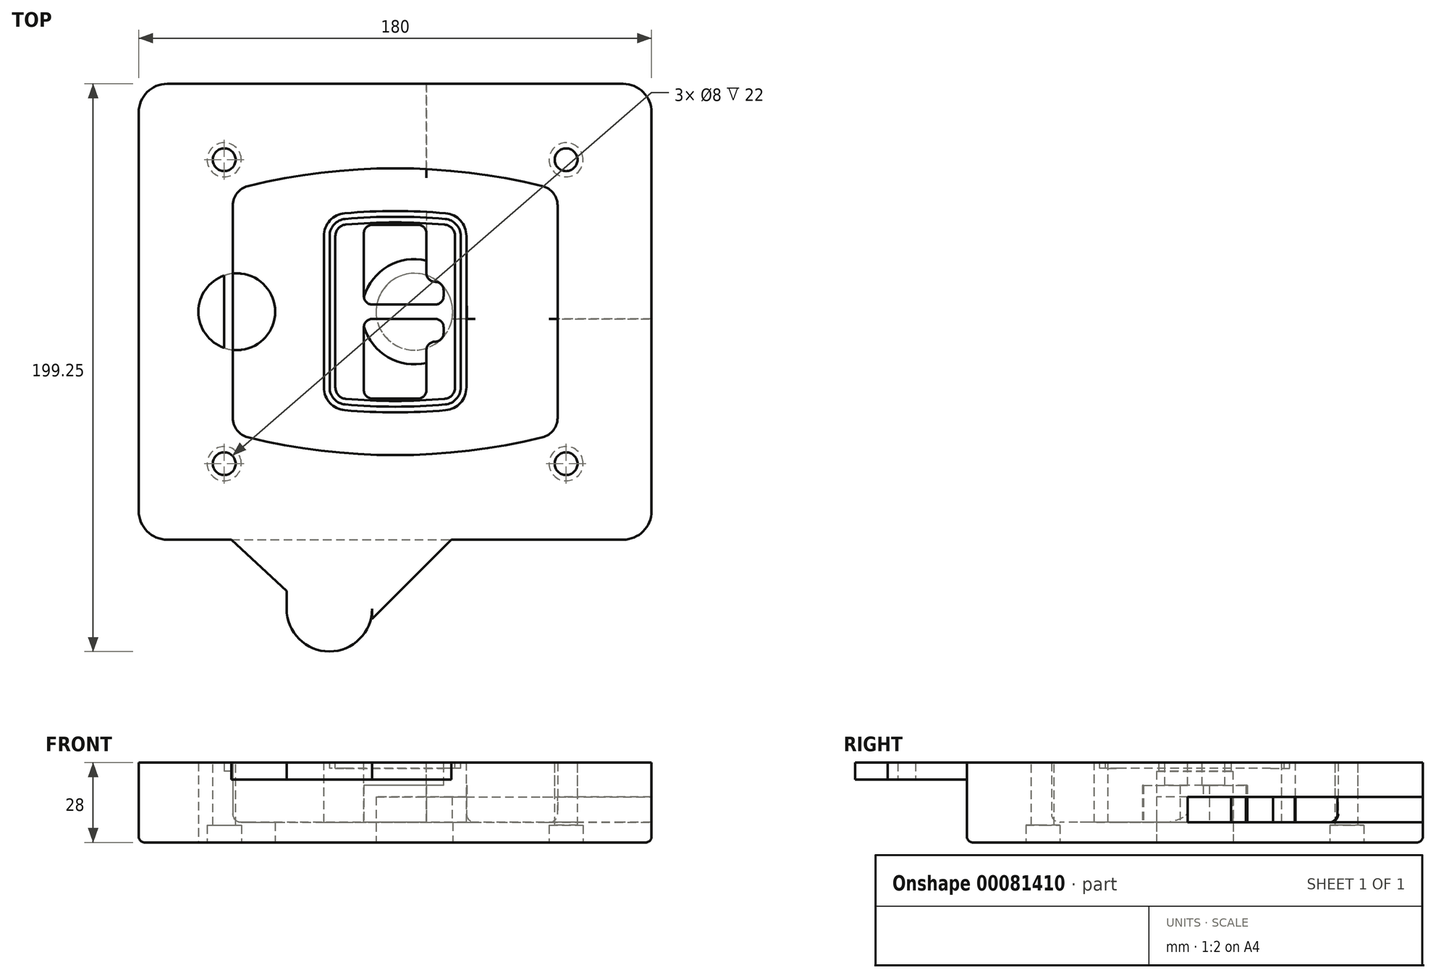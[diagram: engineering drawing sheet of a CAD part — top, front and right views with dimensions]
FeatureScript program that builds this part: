
annotation { "Feature Type Name" : "Feature", "Feature Type Description" : "" }
export const myFeature = defineFeature(function(context is Context, id is Id, definition is map)
    precondition{}
    {
        {
            var Q0;
            Q0=qCreatedBy(makeId("Top.planeOp"),FACE);
            var sketch = newSketch(context, id + "F0", { "sketchPlane" : qUnion([Q0])});
            skPoint(sketch, "E0.rect.middle", {"position": v(0, 0) * mm});
            skLineSegment(sketch, "E1.bottom", {"start": v(-80, -80) * mm, "end": v(80, -80) * mm});
            skLineSegment(sketch, "E1.top", {"start": v(-80, 80) * mm, "end": v(80, 80) * mm});
            skLineSegment(sketch, "E1.left", {"start": v(-90, -70) * mm, "end": v(-90, 70) * mm});
            skLineSegment(sketch, "E1.right", {"start": v(90, -70) * mm, "end": v(90, 70) * mm});
            skLineSegment(sketch, "E2", {"start": v(-90, 80) * mm, "end": v(90, -80) * mm, "construction": true});
            skLineSegment(sketch, "E3", {"start": v(90, 80) * mm, "end": v(-90, -80) * mm, "construction": true});
            skCircle(sketch, "E4", {"center": v(-60, 53.33) * mm, "radius": 4 * mm});
            skCircle(sketch, "E5", {"center": v(60, 53.33) * mm, "radius": 4 * mm});
            skCircle(sketch, "E6", {"center": v(60, -53.33) * mm, "radius": 4 * mm});
            skCircle(sketch, "E7", {"center": v(-60, -53.33) * mm, "radius": 4 * mm});
            skLineSegment(sketch, "E8", {"start": v(-60, 53.33) * mm, "end": v(60, 53.33) * mm, "construction": true});
            skLineSegment(sketch, "E9", {"start": v(60, 53.33) * mm, "end": v(60, -53.33) * mm, "construction": true});
            skLineSegment(sketch, "E10", {"start": v(60, -53.33) * mm, "end": v(-60, -53.33) * mm, "construction": true});
            skLineSegment(sketch, "E11", {"start": v(-60, -53.33) * mm, "end": v(-60, 53.33) * mm, "construction": true});
            skLineSegment(sketch, "E12", {"start": v(-60, 37.3) * mm, "end": v(-60, -37.3) * mm});
            skLineSegment(sketch, "E13", {"start": v(60, 37.3) * mm, "end": v(60, -37.3) * mm});
            skArc(sketch, "E14", {"start": v(52.38, 47.01) * mm, "mid": v(0, 53.33) * mm, "end": v(-52.38, 47.01) * mm});
            skArc(sketch, "E15", {"start": v(-52.38, -47.01) * mm, "mid": v(0, -53.33) * mm, "end": v(52.38, -47.01) * mm});
            skLineSegment(sketch, "E16", {"start": v(-60, 0) * mm, "end": v(60, 0) * mm, "construction": true});
            skPoint(sketch, "E17.visualSharp", {"position": v(-60, -45) * mm});
            skArc(sketch, "E17.filletArc", {"start": v(-60, -37.3) * mm, "mid": v(-57.87, -43.47) * mm, "end": v(-52.38, -47.01) * mm});
            skPoint(sketch, "E18.visualSharp", {"position": v(-60, 45) * mm});
            skArc(sketch, "E18.filletArc", {"start": v(-52.38, 47.01) * mm, "mid": v(-57.87, 43.47) * mm, "end": v(-60, 37.3) * mm});
            skPoint(sketch, "E19.visualSharp", {"position": v(60, 45) * mm});
            skArc(sketch, "E19.filletArc", {"start": v(60, 37.3) * mm, "mid": v(57.87, 43.47) * mm, "end": v(52.38, 47.01) * mm});
            skPoint(sketch, "E20.visualSharp", {"position": v(60, -45) * mm});
            skArc(sketch, "E20.filletArc", {"start": v(52.38, -47.01) * mm, "mid": v(57.87, -43.47) * mm, "end": v(60, -37.3) * mm});
            skPoint(sketch, "E21.visualSharp", {"position": v(-90, 80) * mm});
            skArc(sketch, "E21.filletArc", {"start": v(-80, 80) * mm, "mid": v(-87.07, 77.07) * mm, "end": v(-90, 70) * mm});
            skPoint(sketch, "E22.visualSharp", {"position": v(90, 80) * mm});
            skArc(sketch, "E22.filletArc", {"start": v(90, 70) * mm, "mid": v(87.07, 77.07) * mm, "end": v(80, 80) * mm});
            skPoint(sketch, "E23.visualSharp", {"position": v(90, -80) * mm});
            skArc(sketch, "E23.filletArc", {"start": v(80, -80) * mm, "mid": v(87.07, -77.07) * mm, "end": v(90, -70) * mm});
            skPoint(sketch, "E24.visualSharp", {"position": v(-90, -80) * mm});
            skArc(sketch, "E24.filletArc", {"start": v(-90, -70) * mm, "mid": v(-87.07, -77.07) * mm, "end": v(-80, -80) * mm});
            skArc(sketch, "E25.0", {"start": v(57, 37.3) * mm, "mid": v(55.5, 41.62) * mm, "end": v(51.67, 44.1) * mm});
            skLineSegment(sketch, "E25.1", {"start": v(57, 37.3) * mm, "end": v(57, -37.3) * mm});
            skArc(sketch, "E25.2", {"start": v(51.67, -44.1) * mm, "mid": v(55.5, -41.62) * mm, "end": v(57, -37.3) * mm});
            skArc(sketch, "E25.3", {"start": v(-51.67, -44.1) * mm, "mid": v(0, -50.33) * mm, "end": v(51.67, -44.1) * mm});
            skArc(sketch, "E25.4", {"start": v(-57, -37.3) * mm, "mid": v(-55.5, -41.62) * mm, "end": v(-51.67, -44.1) * mm});
            skArc(sketch, "E25.5", {"start": v(51.67, 44.1) * mm, "mid": v(0, 50.33) * mm, "end": v(-51.67, 44.1) * mm});
            skLineSegment(sketch, "E25.6", {"start": v(-57, 37.3) * mm, "end": v(-57, -37.3) * mm});
            skArc(sketch, "E25.7", {"start": v(-51.67, 44.1) * mm, "mid": v(-55.5, 41.62) * mm, "end": v(-57, 37.3) * mm});
            skArc(sketch, "E26.0", {"start": v(-53.33, 50.9) * mm, "mid": v(-61.01, 45.94) * mm, "end": v(-64, 37.3) * mm});
            skArc(sketch, "E26.1", {"start": v(53.33, 50.9) * mm, "mid": v(0, 57.33) * mm, "end": v(-53.33, 50.9) * mm});
            skArc(sketch, "E26.2", {"start": v(64, 37.3) * mm, "mid": v(61.01, 45.94) * mm, "end": v(53.33, 50.9) * mm});
            skLineSegment(sketch, "E26.3", {"start": v(64, 37.3) * mm, "end": v(64, -37.3) * mm});
            skArc(sketch, "E26.4", {"start": v(53.33, -50.9) * mm, "mid": v(61.01, -45.94) * mm, "end": v(64, -37.3) * mm});
            skLineSegment(sketch, "E26.5", {"start": v(-64, 37.3) * mm, "end": v(-64, -37.3) * mm});
            skArc(sketch, "E26.6", {"start": v(-53.33, -50.9) * mm, "mid": v(0, -57.33) * mm, "end": v(53.33, -50.9) * mm});
            skArc(sketch, "E26.7", {"start": v(-64, -37.3) * mm, "mid": v(-61.01, -45.94) * mm, "end": v(-53.33, -50.9) * mm});
            skSolve(sketch);
        }
        {
            var Q0;
            Q0=makeQuery(id+"F0.imprint","IMPRINT",FACE,{"disambiguationData":[TD([[makeQuery(id+"F0.imprint","IMPRINT",EDGE,{"derivedFrom":sQuery(id+"F0.wireOp",EDGE,"E1.bottom")}),1.0]])]});
            var Q1;
            Q1=makeQuery(id+"F0.imprint","IMPRINT",FACE,{"disambiguationData":[TD([[makeQuery(id+"F0.imprint","IMPRINT",EDGE,{"derivedFrom":sQuery(id+"F0.wireOp",EDGE,"E12")}),1.0]])]});
            var Q2;
            Q2=makeQuery(id+"F0.imprint","IMPRINT",FACE,{"disambiguationData":[TD([[makeQuery(id+"F0.imprint","IMPRINT",EDGE,{"derivedFrom":sQuery(id+"F0.wireOp",EDGE,"E25.0")}),1.0]])]});
            var Q3;
            Q3=makeQuery(id+"F0.imprint","IMPRINT",FACE,{"disambiguationData":[TD([[makeQuery(id+"F0.imprint","IMPRINT",EDGE,{"derivedFrom":sQuery(id+"F0.wireOp",EDGE,"E12")}),-1.0]])]});
            extrude(context, id + "F1", {"entities" : qUnion([Q0, Q1, Q2, Q3]), "oppositeDirection" : true, "depth" : 25 * mm});
        }
        {
            var Q0;
            Q0=makeQuery(id+"F0.imprint","IMPRINT",FACE,{"disambiguationData":[TD([[makeQuery(id+"F0.imprint","IMPRINT",EDGE,{"derivedFrom":sQuery(id+"F0.wireOp",EDGE,"E12")}),1.0]])]});
            extrude(context, id + "F2", {"entities" : qUnion([Q0]), "operationType" : NewBodyOperationType.ADD, "depth" : 3 * mm});
        }
        {
            var Q0;
            Q0=makeQuery(id+"F0.imprint","IMPRINT",FACE,{"disambiguationData":[TD([[makeQuery(id+"F0.imprint","IMPRINT",EDGE,{"derivedFrom":sQuery(id+"F0.wireOp",EDGE,"E25.0")}),1.0]])]});
            extrude(context, id + "F3", {"entities" : qUnion([Q0]), "operationType" : NewBodyOperationType.REMOVE, "oppositeDirection" : true, "depth" : 18 * mm});
        }
        {
            var Q0;
            Q0=makeQuery(id+"F2.opExtrude","CAP_FACE",FACE,{"disambiguationData":[OSD([sQuery(id+"F0.wireOp",EDGE,"E12"),sQuery(id+"F0.wireOp",EDGE,"E13"),sQuery(id+"F0.wireOp",EDGE,"E14"),sQuery(id+"F0.wireOp",EDGE,"E15"),sQuery(id+"F0.wireOp",EDGE,"E17.filletArc"),sQuery(id+"F0.wireOp",EDGE,"E18.filletArc"),sQuery(id+"F0.wireOp",EDGE,"E19.filletArc"),sQuery(id+"F0.wireOp",EDGE,"E20.filletArc"),sQuery(id+"F0.wireOp",EDGE,"E25.0"),sQuery(id+"F0.wireOp",EDGE,"E25.1"),sQuery(id+"F0.wireOp",EDGE,"E25.2"),sQuery(id+"F0.wireOp",EDGE,"E25.3"),sQuery(id+"F0.wireOp",EDGE,"E25.4"),sQuery(id+"F0.wireOp",EDGE,"E25.5"),sQuery(id+"F0.wireOp",EDGE,"E25.6"),sQuery(id+"F0.wireOp",EDGE,"E25.7")])],"isStart":false});
            var sketch = newSketch(context, id + "F4", { "sketchPlane" : qUnion([Q0])});
            skArc(sketch, "E27.0", {"start": v(-17.7, -34.56) * mm, "mid": v(0, -35.33) * mm, "end": v(17.7, -34.56) * mm});
            skArc(sketch, "E28.0", {"start": v(17.7, 34.56) * mm, "mid": v(0, 35.33) * mm, "end": v(-17.7, 34.56) * mm});
            skLineSegment(sketch, "E29", {"start": v(-25, 26.59) * mm, "end": v(-25, -26.59) * mm});
            skLineSegment(sketch, "E30", {"start": v(25, 26.59) * mm, "end": v(25, -26.59) * mm});
            skLineSegment(sketch, "E31", {"start": v(-25, 33.78) * mm, "end": v(25, 33.78) * mm, "construction": true});
            skLineSegment(sketch, "E32", {"start": v(-25, -33.78) * mm, "end": v(25, -33.78) * mm, "construction": true});
            skPoint(sketch, "E33.visualSharp", {"position": v(-25, 33.78) * mm});
            skArc(sketch, "E33.filletArc", {"start": v(-17.7, 34.56) * mm, "mid": v(-22.9, 32) * mm, "end": v(-25, 26.59) * mm});
            skPoint(sketch, "E34.visualSharp", {"position": v(25, 33.78) * mm});
            skArc(sketch, "E34.filletArc", {"start": v(25, 26.59) * mm, "mid": v(22.9, 32) * mm, "end": v(17.7, 34.56) * mm});
            skPoint(sketch, "E35.visualSharp", {"position": v(25, -33.78) * mm});
            skArc(sketch, "E35.filletArc", {"start": v(17.7, -34.56) * mm, "mid": v(22.9, -32) * mm, "end": v(25, -26.59) * mm});
            skPoint(sketch, "E36.visualSharp", {"position": v(-25, -33.78) * mm});
            skArc(sketch, "E36.filletArc", {"start": v(-25, -26.59) * mm, "mid": v(-22.9, -32) * mm, "end": v(-17.7, -34.56) * mm});
            skArc(sketch, "E37.0", {"start": v(51.67, 44.1) * mm, "mid": v(0, 50.33) * mm, "end": v(-51.67, 44.1) * mm});
            skArc(sketch, "E37.1", {"start": v(-51.67, 44.1) * mm, "mid": v(-55.5, 41.62) * mm, "end": v(-57, 37.3) * mm});
            skLineSegment(sketch, "E37.2", {"start": v(-57, 37.3) * mm, "end": v(-57, -37.3) * mm});
            skArc(sketch, "E37.3", {"start": v(-57, -37.3) * mm, "mid": v(-55.5, -41.62) * mm, "end": v(-51.67, -44.1) * mm});
            skArc(sketch, "E37.4", {"start": v(-51.67, -44.1) * mm, "mid": v(0, -50.33) * mm, "end": v(51.67, -44.1) * mm});
            skArc(sketch, "E37.5", {"start": v(51.67, -44.1) * mm, "mid": v(55.5, -41.62) * mm, "end": v(57, -37.3) * mm});
            skLineSegment(sketch, "E37.6", {"start": v(57, 37.3) * mm, "end": v(57, -37.3) * mm});
            skArc(sketch, "E37.7", {"start": v(57, 37.3) * mm, "mid": v(55.5, 41.62) * mm, "end": v(51.67, 44.1) * mm});
            skLineSegment(sketch, "E38.0", {"start": v(23, 26.59) * mm, "end": v(23, -26.59) * mm});
            skArc(sketch, "E38.1", {"start": v(17.53, -32.56) * mm, "mid": v(21.42, -30.64) * mm, "end": v(23, -26.59) * mm});
            skArc(sketch, "E38.2", {"start": v(-17.53, -32.56) * mm, "mid": v(0, -33.33) * mm, "end": v(17.53, -32.56) * mm});
            skArc(sketch, "E38.3", {"start": v(-23, -26.59) * mm, "mid": v(-21.42, -30.64) * mm, "end": v(-17.53, -32.56) * mm});
            skLineSegment(sketch, "E38.4", {"start": v(-23, 26.59) * mm, "end": v(-23, -26.59) * mm});
            skArc(sketch, "E38.5", {"start": v(23, 26.59) * mm, "mid": v(21.42, 30.64) * mm, "end": v(17.53, 32.56) * mm});
            skArc(sketch, "E38.6", {"start": v(-17.53, 32.56) * mm, "mid": v(-21.42, 30.64) * mm, "end": v(-23, 26.59) * mm});
            skArc(sketch, "E38.7", {"start": v(17.53, 32.56) * mm, "mid": v(0, 33.33) * mm, "end": v(-17.53, 32.56) * mm});
            skArc(sketch, "E39.0", {"start": v(21, 26.59) * mm, "mid": v(19.95, 29.29) * mm, "end": v(17.35, 30.57) * mm});
            skLineSegment(sketch, "E39.1", {"start": v(21, 26.59) * mm, "end": v(21, -26.59) * mm});
            skArc(sketch, "E39.2", {"start": v(17.35, -30.57) * mm, "mid": v(19.95, -29.29) * mm, "end": v(21, -26.59) * mm});
            skArc(sketch, "E39.3", {"start": v(-17.35, -30.57) * mm, "mid": v(0, -31.33) * mm, "end": v(17.35, -30.57) * mm});
            skArc(sketch, "E39.4", {"start": v(-21, -26.59) * mm, "mid": v(-19.95, -29.29) * mm, "end": v(-17.35, -30.57) * mm});
            skArc(sketch, "E39.5", {"start": v(17.35, 30.57) * mm, "mid": v(0, 31.33) * mm, "end": v(-17.35, 30.57) * mm});
            skLineSegment(sketch, "E39.6", {"start": v(-21, 26.59) * mm, "end": v(-21, -26.59) * mm});
            skArc(sketch, "E39.7", {"start": v(-17.35, 30.57) * mm, "mid": v(-19.95, 29.29) * mm, "end": v(-21, 26.59) * mm});
            skLineSegment(sketch, "E40", {"start": v(-25, 0) * mm, "end": v(25, 0) * mm, "construction": true});
            skLineSegment(sketch, "E41", {"start": v(-11, 5.5) * mm, "end": v(-11, 27.5) * mm});
            skLineSegment(sketch, "E42", {"start": v(-8, 30.5) * mm, "end": v(8, 30.5) * mm});
            skLineSegment(sketch, "E43", {"start": v(11, 27.5) * mm, "end": v(11, 13.5) * mm});
            skLineSegment(sketch, "E44", {"start": v(14, 10.5) * mm, "end": v(14, 10.5) * mm});
            skLineSegment(sketch, "E45", {"start": v(17, 7.5) * mm, "end": v(17, 5.5) * mm});
            skLineSegment(sketch, "E46", {"start": v(14, 2.5) * mm, "end": v(-8, 2.5) * mm});
            skPoint(sketch, "E47.visualSharp", {"position": v(-11, 30.5) * mm});
            skArc(sketch, "E47.filletArc", {"start": v(-8, 30.5) * mm, "mid": v(-10.12, 29.62) * mm, "end": v(-11, 27.5) * mm});
            skPoint(sketch, "E48.visualSharp", {"position": v(11, 30.5) * mm});
            skArc(sketch, "E48.filletArc", {"start": v(11, 27.5) * mm, "mid": v(10.12, 29.62) * mm, "end": v(8, 30.5) * mm});
            skPoint(sketch, "E49.visualSharp", {"position": v(11, 10.5) * mm});
            skArc(sketch, "E49.filletArc", {"start": v(11, 13.5) * mm, "mid": v(11.88, 11.38) * mm, "end": v(14, 10.5) * mm});
            skPoint(sketch, "E50.visualSharp", {"position": v(17, 10.5) * mm});
            skArc(sketch, "E50.filletArc", {"start": v(17, 7.5) * mm, "mid": v(16.12, 9.62) * mm, "end": v(14, 10.5) * mm});
            skPoint(sketch, "E51.visualSharp", {"position": v(17, 2.5) * mm});
            skArc(sketch, "E51.filletArc", {"start": v(14, 2.5) * mm, "mid": v(16.12, 3.38) * mm, "end": v(17, 5.5) * mm});
            skPoint(sketch, "E52.visualSharp", {"position": v(-11, 2.5) * mm});
            skArc(sketch, "E52.filletArc", {"start": v(-11, 5.5) * mm, "mid": v(-10.12, 3.38) * mm, "end": v(-8, 2.5) * mm});
            skLineSegment(sketch, "E53.0.MirrorCS", {"start": v(14, -2.5) * mm, "end": v(-8, -2.5) * mm});
            skArc(sketch, "E54.0.MirrorCS", {"start": v(-11, -5.5) * mm, "mid": v(-10.12, -3.38) * mm, "end": v(-8, -2.5) * mm});
            skLineSegment(sketch, "E55.0.MirrorCS", {"start": v(-11, -5.5) * mm, "end": v(-11, -27.5) * mm});
            skArc(sketch, "E56.0.MirrorCS", {"start": v(-8, -30.5) * mm, "mid": v(-10.12, -29.62) * mm, "end": v(-11, -27.5) * mm});
            skLineSegment(sketch, "E57.0.MirrorCS", {"start": v(-8, -30.5) * mm, "end": v(8, -30.5) * mm});
            skArc(sketch, "E58.0.MirrorCS", {"start": v(11, -27.5) * mm, "mid": v(10.12, -29.62) * mm, "end": v(8, -30.5) * mm});
            skLineSegment(sketch, "E59.0.MirrorCS", {"start": v(11, -27.5) * mm, "end": v(11, -13.5) * mm});
            skArc(sketch, "E60.0.MirrorCS", {"start": v(11, -13.5) * mm, "mid": v(11.88, -11.38) * mm, "end": v(14, -10.5) * mm});
            skArc(sketch, "E61.0.MirrorCS", {"start": v(17, -7.5) * mm, "mid": v(16.12, -9.62) * mm, "end": v(14, -10.5) * mm});
            skLineSegment(sketch, "E62.0.MirrorCS", {"start": v(17, -7.5) * mm, "end": v(17, -5.5) * mm});
            skArc(sketch, "E63.0.MirrorCS", {"start": v(14, -2.5) * mm, "mid": v(16.12, -3.38) * mm, "end": v(17, -5.5) * mm});
            skSolve(sketch);
        }
        {
            var Q0;
            Q0=makeQuery(id+"F4.imprint","IMPRINT",FACE,{"disambiguationData":[TD([[makeQuery(id+"F4.imprint","IMPRINT",EDGE,{"derivedFrom":sQuery(id+"F4.wireOp",EDGE,"E27.0")}),1.0]])]});
            var Q1;
            Q1=makeQuery(id+"F4.imprint","IMPRINT",FACE,{"disambiguationData":[TD([[makeQuery(id+"F4.imprint","IMPRINT",EDGE,{"derivedFrom":sQuery(id+"F4.wireOp",EDGE,"E38.0")}),-1.0]])]});
            var Q2;
            Q2=makeQuery(id+"F4.imprint","IMPRINT",FACE,{"disambiguationData":[TD([[makeQuery(id+"F4.imprint","IMPRINT",EDGE,{"derivedFrom":sQuery(id+"F4.wireOp",EDGE,"E39.0")}),1.0]])]});
            extrude(context, id + "F5", {"entities" : qUnion([Q0, Q1, Q2]), "operationType" : NewBodyOperationType.ADD, "endBound" : BoundingType.UP_TO_NEXT, "oppositeDirection" : true, "depth" : 25 * mm});
        }
        {
            var Q0;
            Q0=makeQuery(id+"F4.imprint","IMPRINT",FACE,{"disambiguationData":[TD([[makeQuery(id+"F4.imprint","IMPRINT",EDGE,{"derivedFrom":sQuery(id+"F4.wireOp",EDGE,"E38.0")}),-1.0]])]});
            extrude(context, id + "F6", {"entities" : qUnion([Q0]), "operationType" : NewBodyOperationType.REMOVE, "oppositeDirection" : true, "depth" : 2 * mm});
        }
        {
            var Q0;
            Q0=makeQuery(id+"F1.opExtrude","CAP_FACE",FACE,{"disambiguationData":[OSD([sQuery(id+"F0.wireOp",EDGE,"E1.bottom"),sQuery(id+"F0.wireOp",EDGE,"E1.top"),sQuery(id+"F0.wireOp",EDGE,"E1.left"),sQuery(id+"F0.wireOp",EDGE,"E1.right"),sQuery(id+"F0.wireOp",EDGE,"E4"),sQuery(id+"F0.wireOp",EDGE,"E5"),sQuery(id+"F0.wireOp",EDGE,"E6"),sQuery(id+"F0.wireOp",EDGE,"E7"),sQuery(id+"F0.wireOp",EDGE,"E21.filletArc"),sQuery(id+"F0.wireOp",EDGE,"E22.filletArc"),sQuery(id+"F0.wireOp",EDGE,"E23.filletArc"),sQuery(id+"F0.wireOp",EDGE,"E24.filletArc")])],"isStart":false});
            var sketch = newSketch(context, id + "F7", { "sketchPlane" : qUnion([Q0])});
            skCircle(sketch, "E64", {"center": v(6.76, 0) * mm, "radius": 13.47 * mm});
            skCircle(sketch, "E65", {"center": v(-55.56, 0) * mm, "radius": 13.47 * mm});
            skLineSegment(sketch, "E66", {"start": v(90, 0) * mm, "end": v(-90, 0) * mm});
            skCircle(sketch, "E67", {"center": v(6.76, 0) * mm, "radius": 18.47 * mm});
            skCircle(sketch, "E68", {"center": v(60, -53.33) * mm, "radius": 6 * mm});
            skCircle(sketch, "E69", {"center": v(-60, -53.33) * mm, "radius": 6 * mm});
            skCircle(sketch, "E70", {"center": v(-60, 53.33) * mm, "radius": 6 * mm});
            skCircle(sketch, "E71", {"center": v(60, 53.33) * mm, "radius": 6 * mm});
            skSolve(sketch);
        }
        {
            var Q0;
            {var subQ1=sQuery(id+"F7.wireOp",EDGE,"E66");var subQ4=sQuery(id+"F7.wireOp",EDGE,"E64");var subQ6=makeQuery(id+"F7.imprint","INTERSECT",VERTEX,{"disambiguationData":[OD(0.0)],"derivedFrom":[subQ4,subQ1]});Q0=makeQuery(id+"F7.imprint","IMPRINT",FACE,{"disambiguationData":[TD([[makeQuery(id+"F7.imprint","IMPRINT",EDGE,{"disambiguationData":[TD([[subQ6,-1.0]])],"derivedFrom":subQ4}),-1.0]])]});}
            var Q1;
            {var subQ0=sQuery(id+"F7.wireOp",EDGE,"E66");var subQ1=sQuery(id+"F7.wireOp",EDGE,"E64");var subQ3=makeQuery(id+"F7.imprint","INTERSECT",VERTEX,{"disambiguationData":[OD(0.0)],"derivedFrom":[subQ1,subQ0]});Q1=makeQuery(id+"F7.imprint","IMPRINT",FACE,{"disambiguationData":[TD([[makeQuery(id+"F7.imprint","IMPRINT",EDGE,{"disambiguationData":[TD([[subQ3,-1.0]])],"derivedFrom":subQ1}),1.0]])]});}
            var Q2;
            {var subQ0=sQuery(id+"F7.wireOp",EDGE,"E66");var subQ1=sQuery(id+"F7.wireOp",EDGE,"E64");var subQ3=makeQuery(id+"F7.imprint","INTERSECT",VERTEX,{"disambiguationData":[OD(0.0)],"derivedFrom":[subQ1,subQ0]});Q2=makeQuery(id+"F7.imprint","IMPRINT",FACE,{"disambiguationData":[TD([[makeQuery(id+"F7.imprint","IMPRINT",EDGE,{"disambiguationData":[TD([[subQ3,1.0]])],"derivedFrom":subQ1}),1.0]])]});}
            var Q3;
            {var subQ1=sQuery(id+"F7.wireOp",EDGE,"E66");var subQ4=sQuery(id+"F7.wireOp",EDGE,"E64");var subQ6=makeQuery(id+"F7.imprint","INTERSECT",VERTEX,{"disambiguationData":[OD(0.0)],"derivedFrom":[subQ4,subQ1]});Q3=makeQuery(id+"F7.imprint","IMPRINT",FACE,{"disambiguationData":[TD([[makeQuery(id+"F7.imprint","IMPRINT",EDGE,{"disambiguationData":[TD([[subQ6,1.0]])],"derivedFrom":subQ4}),-1.0]])]});}
            extrude(context, id + "F8", {"entities" : qUnion([Q0, Q1, Q2, Q3]), "operationType" : NewBodyOperationType.ADD, "oppositeDirection" : true, "depth" : 20 * mm});
        }
        {
            var Q0;
            {var subQ0=sQuery(id+"F7.wireOp",EDGE,"E66");var subQ1=sQuery(id+"F7.wireOp",EDGE,"E64");var subQ3=makeQuery(id+"F7.imprint","INTERSECT",VERTEX,{"disambiguationData":[OD(0.0)],"derivedFrom":[subQ1,subQ0]});Q0=makeQuery(id+"F7.imprint","IMPRINT",FACE,{"disambiguationData":[TD([[makeQuery(id+"F7.imprint","IMPRINT",EDGE,{"disambiguationData":[TD([[subQ3,-1.0]])],"derivedFrom":subQ1}),1.0]])]});}
            var Q1;
            {var subQ0=sQuery(id+"F7.wireOp",EDGE,"E66");var subQ1=sQuery(id+"F7.wireOp",EDGE,"E64");var subQ3=makeQuery(id+"F7.imprint","INTERSECT",VERTEX,{"disambiguationData":[OD(0.0)],"derivedFrom":[subQ1,subQ0]});Q1=makeQuery(id+"F7.imprint","IMPRINT",FACE,{"disambiguationData":[TD([[makeQuery(id+"F7.imprint","IMPRINT",EDGE,{"disambiguationData":[TD([[subQ3,1.0]])],"derivedFrom":subQ1}),1.0]])]});}
            extrude(context, id + "F9", {"entities" : qUnion([Q0, Q1]), "operationType" : NewBodyOperationType.REMOVE, "oppositeDirection" : true, "depth" : 16 * mm});
        }
        {
            var Q0;
            {var subQ0=sQuery(id+"F7.wireOp",EDGE,"E66");var subQ1=sQuery(id+"F7.wireOp",EDGE,"E65");var subQ3=makeQuery(id+"F7.imprint","INTERSECT",VERTEX,{"disambiguationData":[OD(0.0)],"derivedFrom":[subQ1,subQ0]});Q0=makeQuery(id+"F7.imprint","IMPRINT",FACE,{"disambiguationData":[TD([[makeQuery(id+"F7.imprint","IMPRINT",EDGE,{"disambiguationData":[TD([[subQ3,-1.0]])],"derivedFrom":subQ1}),1.0]])]});}
            var Q1;
            {var subQ0=sQuery(id+"F7.wireOp",EDGE,"E66");var subQ1=sQuery(id+"F7.wireOp",EDGE,"E65");var subQ3=makeQuery(id+"F7.imprint","INTERSECT",VERTEX,{"disambiguationData":[OD(0.0)],"derivedFrom":[subQ1,subQ0]});Q1=makeQuery(id+"F7.imprint","IMPRINT",FACE,{"disambiguationData":[TD([[makeQuery(id+"F7.imprint","IMPRINT",EDGE,{"disambiguationData":[TD([[subQ3,1.0]])],"derivedFrom":subQ1}),1.0]])]});}
            extrude(context, id + "F10", {"entities" : qUnion([Q0, Q1]), "operationType" : NewBodyOperationType.REMOVE, "oppositeDirection" : true, "depth" : 25 * mm});
        }
        {
            var Q0;
            Q0=makeQuery(id+"F7.imprint","IMPRINT",FACE,{"disambiguationData":[TD([[makeQuery(id+"F7.imprint","IMPRINT",EDGE,{"derivedFrom":sQuery(id+"F7.wireOp",EDGE,"E68")}),1.0]])]});
            var Q1;
            Q1=makeQuery(id+"F7.imprint","IMPRINT",FACE,{"disambiguationData":[TD([[makeQuery(id+"F7.imprint","IMPRINT",EDGE,{"derivedFrom":makeQuery(id+"F1.opExtrude","CAP_EDGE",EDGE,{"disambiguationData":[OSD([sQuery(id+"F0.wireOp",EDGE,"E5")])],"isStart":false})}),-1.0]])]});
            var Q2;
            Q2=makeQuery(id+"F7.imprint","IMPRINT",FACE,{"disambiguationData":[TD([[makeQuery(id+"F7.imprint","IMPRINT",EDGE,{"derivedFrom":sQuery(id+"F7.wireOp",EDGE,"E69")}),1.0]])]});
            var Q3;
            Q3=makeQuery(id+"F7.imprint","IMPRINT",FACE,{"disambiguationData":[TD([[makeQuery(id+"F7.imprint","IMPRINT",EDGE,{"derivedFrom":makeQuery(id+"F1.opExtrude","CAP_EDGE",EDGE,{"disambiguationData":[OSD([sQuery(id+"F0.wireOp",EDGE,"E4")])],"isStart":false})}),-1.0]])]});
            var Q4;
            Q4=makeQuery(id+"F7.imprint","IMPRINT",FACE,{"disambiguationData":[TD([[makeQuery(id+"F7.imprint","IMPRINT",EDGE,{"derivedFrom":sQuery(id+"F7.wireOp",EDGE,"E70")}),1.0]])]});
            var Q5;
            Q5=makeQuery(id+"F7.imprint","IMPRINT",FACE,{"disambiguationData":[TD([[makeQuery(id+"F7.imprint","IMPRINT",EDGE,{"derivedFrom":makeQuery(id+"F1.opExtrude","CAP_EDGE",EDGE,{"disambiguationData":[OSD([sQuery(id+"F0.wireOp",EDGE,"E7")])],"isStart":false})}),-1.0]])]});
            var Q6;
            Q6=makeQuery(id+"F7.imprint","IMPRINT",FACE,{"disambiguationData":[TD([[makeQuery(id+"F7.imprint","IMPRINT",EDGE,{"derivedFrom":sQuery(id+"F7.wireOp",EDGE,"E71")}),1.0]])]});
            var Q7;
            Q7=makeQuery(id+"F7.imprint","IMPRINT",FACE,{"disambiguationData":[TD([[makeQuery(id+"F7.imprint","IMPRINT",EDGE,{"derivedFrom":makeQuery(id+"F1.opExtrude","CAP_EDGE",EDGE,{"disambiguationData":[OSD([sQuery(id+"F0.wireOp",EDGE,"E6")])],"isStart":false})}),-1.0]])]});
            extrude(context, id + "F11", {"entities" : qUnion([Q0, Q1, Q2, Q3, Q4, Q5, Q6, Q7]), "operationType" : NewBodyOperationType.REMOVE, "oppositeDirection" : true, "depth" : 6 * mm});
        }
        {
            var Q0;
            Q0=makeQuery(id+"F9.boolean.opBoolean","COPY",FACE,{"derivedFrom":makeQuery(id+"F9.opExtrude","CAP_FACE",FACE,{"disambiguationData":[OSD([sQuery(id+"F7.wireOp",EDGE,"E64")])],"isStart":false})});
            var sketch = newSketch(context, id + "F12", { "sketchPlane" : qUnion([Q0])});
            skArc(sketch, "E72.0", {"start": v(11, -88.19) * mm, "mid": v(97.1, -83.6) * mm, "end": v(92.5, 2.5) * mm});
            skLineSegment(sketch, "E72.1", {"start": v(11, -17.97) * mm, "end": v(11, -17.97) * mm});
            skLineSegment(sketch, "E73", {"start": v(92.5, -105.13) * mm, "end": v(102.3, -105.13) * mm});
            skLineSegment(sketch, "E74.0", {"start": v(92.5, 2.5) * mm, "end": v(14, 2.5) * mm});
            skArc(sketch, "E74.1", {"start": v(14, 2.5) * mm, "mid": v(16.12, 3.38) * mm, "end": v(17, 5.5) * mm});
            skLineSegment(sketch, "E74.2", {"start": v(17, 7.5) * mm, "end": v(17, 5.5) * mm});
            skArc(sketch, "E74.3", {"start": v(17, 7.5) * mm, "mid": v(16.12, 9.62) * mm, "end": v(14, 10.5) * mm});
            skArc(sketch, "E74.4", {"start": v(11, 13.5) * mm, "mid": v(11.88, 11.38) * mm, "end": v(14, 10.5) * mm});
            skLineSegment(sketch, "E74.5", {"start": v(11, 13.5) * mm, "end": v(11, -88.19) * mm});
            skLineSegment(sketch, "E74.7", {"start": v(92.5, -2.5) * mm, "end": v(14, -2.5) * mm});
            skArc(sketch, "E74.8", {"start": v(14, -2.5) * mm, "mid": v(16.12, -3.38) * mm, "end": v(17, -5.5) * mm});
            skLineSegment(sketch, "E74.9", {"start": v(17, -7.5) * mm, "end": v(17, -5.5) * mm});
            skArc(sketch, "E74.10", {"start": v(17, -7.5) * mm, "mid": v(16.12, -9.62) * mm, "end": v(14, -10.5) * mm});
            skArc(sketch, "E74.11", {"start": v(11, -13.5) * mm, "mid": v(11.88, -11.38) * mm, "end": v(14, -10.5) * mm});
            skLineSegment(sketch, "E74.12", {"start": v(11, -17.97) * mm, "end": v(11, -13.5) * mm});
            skPoint(sketch, "E75.orphan", {"position": v(11, -27.5) * mm});
            skPoint(sketch, "E76.orphan", {"position": v(-8, -2.5) * mm});
            skPoint(sketch, "E77.orphan", {"position": v(-8, 2.5) * mm});
            skPoint(sketch, "E78.orphan", {"position": v(11, 27.5) * mm});
            skSolve(sketch);
        }
        {
            var Q0;
            {var subQ7=sQuery(id+"F12.wireOp",EDGE,"E72.0");var subQ14=sQuery(id+"F12.wireOp",EDGE,"E72.1");var subQ16=sQuery(id+"F12.wireOp",EDGE,"E74.1");var subQ18=sQuery(id+"F12.wireOp",EDGE,"E74.8");Q0=qUnion([makeQuery(id+"F12.imprint","IMPRINT",FACE,{"disambiguationData":[TD([[makeQuery(id+"F12.imprint","IMPRINT",EDGE,{"derivedFrom":subQ7}),1.0]])]}),makeQuery(id+"F12.imprint","IMPRINT",FACE,{"disambiguationData":[TD([[makeQuery(id+"F12.imprint","IMPRINT",EDGE,{"derivedFrom":subQ14}),1.0]])]}),makeQuery(id+"F12.imprint","IMPRINT",FACE,{"disambiguationData":[TD([[makeQuery(id+"F12.imprint","IMPRINT",EDGE,{"derivedFrom":subQ16}),1.0]])]}),makeQuery(id+"F12.imprint","IMPRINT",FACE,{"disambiguationData":[TD([[makeQuery(id+"F12.imprint","IMPRINT",EDGE,{"derivedFrom":subQ18}),-1.0]])]})]);}
            var Q1;
            Q1=makeQuery(id+"F5.boolean.opBoolean","SPLIT",FACE,{"disambiguationData":[TD([makeQuery(id+"F5.opExtrude","SWEPT_FACE",FACE,{"disambiguationData":[OSD([sQuery(id+"F4.wireOp",EDGE,"E41")])]})])],"derivedFrom":makeQuery(id+"F3.boolean.opBoolean","COPY",FACE,{"derivedFrom":makeQuery(id+"F3.opExtrude","CAP_FACE",FACE,{"disambiguationData":[OSD([sQuery(id+"F0.wireOp",EDGE,"E25.0"),sQuery(id+"F0.wireOp",EDGE,"E25.1"),sQuery(id+"F0.wireOp",EDGE,"E25.2"),sQuery(id+"F0.wireOp",EDGE,"E25.3"),sQuery(id+"F0.wireOp",EDGE,"E25.4"),sQuery(id+"F0.wireOp",EDGE,"E25.5"),sQuery(id+"F0.wireOp",EDGE,"E25.6"),sQuery(id+"F0.wireOp",EDGE,"E25.7")])],"isStart":false})})});
            extrude(context, id + "F13", {"entities" : qUnion([Q0]), "operationType" : NewBodyOperationType.REMOVE, "endBound" : BoundingType.UP_TO_SURFACE, "endBoundEntityFace" : qUnion([Q1]), "depth" : 25 * mm});
        }
        {
            var Q0;
            Q0=makeQuery(id+"F3.boolean.opBoolean","COPY",EDGE,{"derivedFrom":makeQuery(id+"F3.opExtrude","CAP_EDGE",EDGE,{"disambiguationData":[OSD([sQuery(id+"F0.wireOp",EDGE,"E25.6")])],"isStart":false})});
            var Q1;
            Q1=makeQuery(id+"F8.boolean.opBoolean","INTERSECT",EDGE,{"derivedFrom":[makeQuery(id+"F5.opExtrude","SWEPT_FACE",FACE,{"disambiguationData":[OSD([sQuery(id+"F4.wireOp",EDGE,"E30")])]}),makeQuery(id+"F8.opExtrude","CAP_FACE",FACE,{"disambiguationData":[OSD([sQuery(id+"F7.wireOp",EDGE,"E67")])],"isStart":false})]});
            var Q2;
            Q2=makeQuery(id+"F8.boolean.opBoolean","INTERSECT",EDGE,{"disambiguationData":[OD(1.0)],"derivedFrom":[makeQuery(id+"F5.opExtrude","SWEPT_FACE",FACE,{"disambiguationData":[OSD([sQuery(id+"F4.wireOp",EDGE,"E30")])]}),makeQuery(id+"F8.opExtrude","SWEPT_FACE",FACE,{"disambiguationData":[OSD([sQuery(id+"F7.wireOp",EDGE,"E67")])]})]});
            var Q3;
            {var subQ0=makeQuery(id+"F3.boolean.opBoolean","COPY",FACE,{"derivedFrom":makeQuery(id+"F3.opExtrude","CAP_FACE",FACE,{"disambiguationData":[OSD([sQuery(id+"F0.wireOp",EDGE,"E25.0"),sQuery(id+"F0.wireOp",EDGE,"E25.1"),sQuery(id+"F0.wireOp",EDGE,"E25.2"),sQuery(id+"F0.wireOp",EDGE,"E25.3"),sQuery(id+"F0.wireOp",EDGE,"E25.4"),sQuery(id+"F0.wireOp",EDGE,"E25.5"),sQuery(id+"F0.wireOp",EDGE,"E25.6"),sQuery(id+"F0.wireOp",EDGE,"E25.7")])],"isStart":false})});var subQ1=sQuery(id+"F4.wireOp",EDGE,"E30");Q3=makeQuery(id+"F8.boolean.opBoolean","SPLIT",EDGE,{"disambiguationData":[TD([makeQuery(id+"F5.opExtrude","SWEPT_FACE",FACE,{"disambiguationData":[OSD([sQuery(id+"F4.wireOp",EDGE,"E35.filletArc")])]})])],"derivedFrom":makeQuery(id+"F5.opExtrude","TWEAK_EDGE",EDGE,{"derivedFrom":[subQ0,makeQuery(id+"F4.imprint","IMPRINT",EDGE,{"derivedFrom":subQ1})]})});}
            var Q4;
            {var subQ0=sQuery(id+"F0.wireOp",EDGE,"E25.0");var subQ1=sQuery(id+"F0.wireOp",EDGE,"E25.1");var subQ2=sQuery(id+"F0.wireOp",EDGE,"E25.2");var subQ3=sQuery(id+"F0.wireOp",EDGE,"E25.3");var subQ4=sQuery(id+"F0.wireOp",EDGE,"E25.4");var subQ5=sQuery(id+"F0.wireOp",EDGE,"E25.5");var subQ6=sQuery(id+"F0.wireOp",EDGE,"E25.6");var subQ7=sQuery(id+"F0.wireOp",EDGE,"E25.7");Q4=makeQuery(id+"F8.boolean.opBoolean","INTERSECT",EDGE,{"derivedFrom":[makeQuery(id+"F5.boolean.opBoolean","SPLIT",FACE,{"disambiguationData":[TD([makeQuery(id+"F2.opExtrude","SWEPT_FACE",FACE,{"disambiguationData":[OSD([subQ0])]})])],"derivedFrom":makeQuery(id+"F3.boolean.opBoolean","COPY",FACE,{"derivedFrom":makeQuery(id+"F3.opExtrude","CAP_FACE",FACE,{"disambiguationData":[OSD([subQ0,subQ1,subQ2,subQ3,subQ4,subQ5,subQ6,subQ7])],"isStart":false})})}),makeQuery(id+"F8.opExtrude","SWEPT_FACE",FACE,{"disambiguationData":[OSD([sQuery(id+"F7.wireOp",EDGE,"E67")])]})]});}
            var Q5;
            Q5=makeQuery(id+"F8.boolean.opBoolean","INTERSECT",EDGE,{"disambiguationData":[OD(0.0)],"derivedFrom":[makeQuery(id+"F5.opExtrude","SWEPT_FACE",FACE,{"disambiguationData":[OSD([sQuery(id+"F4.wireOp",EDGE,"E30")])]}),makeQuery(id+"F8.opExtrude","SWEPT_FACE",FACE,{"disambiguationData":[OSD([sQuery(id+"F7.wireOp",EDGE,"E67")])]})]});
            fillet(context, id + "F14", {"entities" : qUnion([Q0, Q1, Q2, Q3, Q4, Q5]), "radius" : 3 * mm, "tangentPropagation" : true, "allowEdgeOverflow" : false});
        }
        {
            var Q0;
            Q0=makeQuery(id+"F1.opExtrude","CAP_EDGE",EDGE,{"disambiguationData":[OSD([sQuery(id+"F0.wireOp",EDGE,"E1.bottom")])],"isStart":false});
            fillet(context, id + "F15", {"entities" : qUnion([Q0]), "radius" : 2 * mm, "tangentPropagation" : true, "allowEdgeOverflow" : false});
        }
        {
            var Q0;
            {var subQ0=sQuery(id+"F0.wireOp",EDGE,"E22.filletArc");var subQ1=sQuery(id+"F0.wireOp",EDGE,"E7");var subQ2=sQuery(id+"F0.wireOp",EDGE,"E6");var subQ3=sQuery(id+"F0.wireOp",EDGE,"E5");var subQ4=sQuery(id+"F0.wireOp",EDGE,"E4");var subQ5=sQuery(id+"F0.wireOp",EDGE,"E1.bottom");var subQ6=sQuery(id+"F0.wireOp",EDGE,"E21.filletArc");var subQ7=sQuery(id+"F0.wireOp",EDGE,"E1.top");var subQ8=sQuery(id+"F0.wireOp",EDGE,"E1.left");var subQ9=sQuery(id+"F0.wireOp",EDGE,"E1.right");var subQ10=sQuery(id+"F0.wireOp",EDGE,"E23.filletArc");var subQ11=sQuery(id+"F0.wireOp",EDGE,"E24.filletArc");Q0=makeQuery(id+"F2.boolean.opBoolean","SPLIT",FACE,{"disambiguationData":[TD([makeQuery(id+"F1.opExtrude","SWEPT_FACE",FACE,{"disambiguationData":[OSD([subQ5])]})])],"derivedFrom":makeQuery(id+"F1.opExtrude","CAP_FACE",FACE,{"disambiguationData":[OSD([subQ5,subQ7,subQ8,subQ9,subQ4,subQ3,subQ2,subQ1,subQ6,subQ0,subQ10,subQ11])],"isStart":true})});}
            var sketch = newSketch(context, id + "F16", { "sketchPlane" : qUnion([Q0])});
            skLineSegment(sketch, "E79.0", {"start": v(-90, -70) * mm, "end": v(-90, 70) * mm});
            skArc(sketch, "E79.1", {"start": v(-90, -70) * mm, "mid": v(-87.07, -77.07) * mm, "end": v(-80, -80) * mm});
            skLineSegment(sketch, "E79.2", {"start": v(-80, -80) * mm, "end": v(80, -80) * mm});
            skArc(sketch, "E79.3", {"start": v(80, -80) * mm, "mid": v(87.07, -77.07) * mm, "end": v(90, -70) * mm});
            skLineSegment(sketch, "E79.4", {"start": v(90, -70) * mm, "end": v(90, 70) * mm});
            skArc(sketch, "E79.5", {"start": v(90, 70) * mm, "mid": v(87.07, 77.07) * mm, "end": v(80, 80) * mm});
            skLineSegment(sketch, "E79.6", {"start": v(-80, 80) * mm, "end": v(80, 80) * mm});
            skArc(sketch, "E79.7", {"start": v(-80, 80) * mm, "mid": v(-87.07, 77.07) * mm, "end": v(-90, 70) * mm});
            skArc(sketch, "E79.8", {"start": v(-42.45, 3.08) * mm, "mid": v(-69.03, 0) * mm, "end": v(-42.45, -3.08) * mm});
            skCircle(sketch, "E79.9", {"center": v(-60, 53.33) * mm, "radius": 4 * mm});
            skCircle(sketch, "E79.10", {"center": v(-60, -53.33) * mm, "radius": 4 * mm});
            skCircle(sketch, "E79.11", {"center": v(60, -53.33) * mm, "radius": 4 * mm});
            skCircle(sketch, "E79.12", {"center": v(60, 53.33) * mm, "radius": 4 * mm});
            skLineSegment(sketch, "E79.13", {"start": v(-60, 37.3) * mm, "end": v(-60, -37.3) * mm});
            skArc(sketch, "E79.14", {"start": v(-52.38, 47.01) * mm, "mid": v(-57.87, 43.47) * mm, "end": v(-60, 37.3) * mm});
            skArc(sketch, "E79.15", {"start": v(52.38, 47.01) * mm, "mid": v(0, 53.33) * mm, "end": v(-52.38, 47.01) * mm});
            skArc(sketch, "E79.16", {"start": v(60, 37.3) * mm, "mid": v(57.87, 43.47) * mm, "end": v(52.38, 47.01) * mm});
            skLineSegment(sketch, "E79.17", {"start": v(60, 37.3) * mm, "end": v(60, -37.3) * mm});
            skArc(sketch, "E79.18", {"start": v(52.38, -47.01) * mm, "mid": v(57.87, -43.47) * mm, "end": v(60, -37.3) * mm});
            skArc(sketch, "E79.19", {"start": v(-52.38, -47.01) * mm, "mid": v(0, -53.33) * mm, "end": v(52.38, -47.01) * mm});
            skArc(sketch, "E79.20", {"start": v(-60, -37.3) * mm, "mid": v(-57.87, -43.47) * mm, "end": v(-52.38, -47.01) * mm});
            skPoint(sketch, "E80.endSnap0", {"position": v(0, 80) * mm});
            skCircle(sketch, "E81", {"center": v(0, 110) * mm, "radius": 6 * mm});
            skLineSegment(sketch, "E82", {"start": v(-57.53, 80) * mm, "end": v(-38.1, 98) * mm});
            skLineSegment(sketch, "E83", {"start": v(-38.1, 98) * mm, "end": v(-38.1, 104.25) * mm});
            skLineSegment(sketch, "E84", {"start": v(19.73, 80) * mm, "end": v(-8.1, 107.83) * mm});
            skLineSegment(sketch, "E85", {"start": v(-8.1, 104.25) * mm, "end": v(-8.1, 107.83) * mm});
            skLineSegment(sketch, "E86", {"start": v(0, 80) * mm, "end": v(0, 110) * mm, "construction": true});
            skArc(sketch, "E87", {"start": v(-8.1, 104.25) * mm, "mid": v(-23.1, 119.25) * mm, "end": v(-38.1, 104.25) * mm});
            skLineSegment(sketch, "E88", {"start": v(-90, 0) * mm, "end": v(90, 0) * mm, "construction": true});
            skLineSegment(sketch, "E89.MirrorCS", {"start": v(19.73, -80) * mm, "end": v(-8.1, -107.83) * mm});
            skLineSegment(sketch, "E90.MirrorCS", {"start": v(-8.1, -104.25) * mm, "end": v(-8.1, -107.83) * mm});
            skArc(sketch, "E91.MirrorCS", {"start": v(-8.1, -104.25) * mm, "mid": v(-23.1, -119.25) * mm, "end": v(-38.1, -104.25) * mm});
            skLineSegment(sketch, "E92.MirrorCS", {"start": v(-38.1, -98) * mm, "end": v(-38.1, -104.25) * mm});
            skLineSegment(sketch, "E93.MirrorCS", {"start": v(-57.53, -80) * mm, "end": v(-38.1, -98) * mm});
            skLineSegment(sketch, "E94.MirrorCS", {"start": v(0, -80) * mm, "end": v(0, -110) * mm, "construction": true});
            skCircle(sketch, "E95.MirrorC", {"center": v(0, -110) * mm, "radius": 6 * mm});
            skSolve(sketch);
        }
        {
            var Q0;
            Q0=makeQuery(id+"F16.imprint","IMPRINT",FACE,{"disambiguationData":[TD([[makeQuery(id+"F16.imprint","IMPRINT",EDGE,{"derivedFrom":sQuery(id+"F16.wireOp",EDGE,"E79.0")}),-1.0]])]});
            var Q1;
            Q1=makeQuery(id+"F16.imprint","IMPRINT",FACE,{"disambiguationData":[TD([[makeQuery(id+"F16.imprint","IMPRINT",EDGE,{"derivedFrom":sQuery(id+"F16.wireOp",EDGE,"E81")}),-1.0]])]});
            var Q2;
            {var subQ0=sQuery(id+"F16.wireOp",EDGE,"E89.MirrorCS");Q2=makeQuery(id+"F16.imprint","IMPRINT",FACE,{"disambiguationData":[TD([[makeQuery(id+"F16.imprint","IMPRINT",EDGE,{"derivedFrom":subQ0}),-1.0]])]});}
            extrude(context, id + "F17", {"entities" : qUnion([Q0, Q1, Q2]), "operationType" : NewBodyOperationType.ADD, "endBound" : BoundingType.SYMMETRIC, "depth" : 6 * mm});
        }
    });
